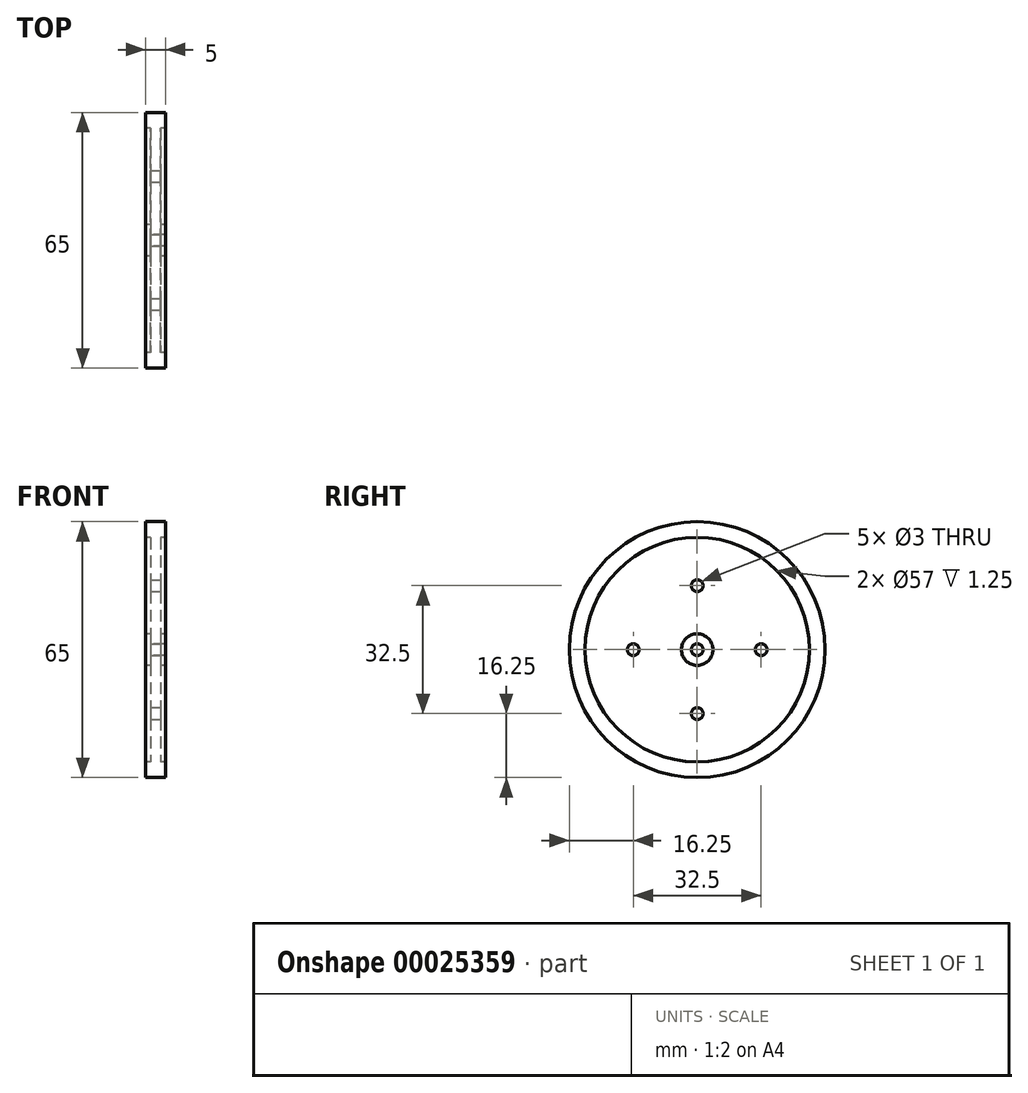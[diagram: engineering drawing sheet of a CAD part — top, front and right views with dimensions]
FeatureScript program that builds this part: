
annotation { "Feature Type Name" : "Feature", "Feature Type Description" : "" }
export const myFeature = defineFeature(function(context is Context, id is Id, definition is map)
    precondition{}
    {
        {
            var Q0;
            Q0=qCreatedBy(makeId("Front.planeOp"),FACE);
            var sketch = newSketch(context, id + "F0", { "sketchPlane" : qUnion([Q0])});
            skLineSegment(sketch, "E0", {"start": v(-50.28, 0) * mm, "end": v(50.2, 0) * mm, "construction": true});
            skLineSegment(sketch, "E1.rect.bottom", {"start": v(2.5, 4) * mm, "end": v(-2.5, 4) * mm});
            skLineSegment(sketch, "E1.rect.top", {"start": v(2.5, 1.5) * mm, "end": v(-2.5, 1.5) * mm});
            skLineSegment(sketch, "E1.rect.left", {"start": v(2.5, 4) * mm, "end": v(2.5, 1.5) * mm});
            skLineSegment(sketch, "E1.rect.right", {"start": v(-2.5, 4) * mm, "end": v(-2.5, 1.5) * mm});
            skPoint(sketch, "E1.rect.middle", {"position": v(0, 2.75) * mm});
            skLineSegment(sketch, "E2.bottom", {"start": v(-1.25, 4) * mm, "end": v(1.25, 4) * mm});
            skLineSegment(sketch, "E2.top", {"start": v(-1.25, 28.5) * mm, "end": v(1.25, 28.5) * mm});
            skLineSegment(sketch, "E2.left", {"start": v(-1.25, 4) * mm, "end": v(-1.25, 28.5) * mm});
            skLineSegment(sketch, "E2.right", {"start": v(1.25, 4) * mm, "end": v(1.25, 28.5) * mm});
            skLineSegment(sketch, "E3.rect.bottom", {"start": v(2.5, 28.5) * mm, "end": v(-2.5, 28.5) * mm});
            skLineSegment(sketch, "E3.rect.top", {"start": v(2.5, 32.5) * mm, "end": v(-2.5, 32.5) * mm});
            skLineSegment(sketch, "E3.rect.left", {"start": v(2.5, 28.5) * mm, "end": v(2.5, 32.5) * mm});
            skLineSegment(sketch, "E3.rect.right", {"start": v(-2.5, 28.5) * mm, "end": v(-2.5, 32.5) * mm});
            skPoint(sketch, "E3.rect.middle", {"position": v(0, 30.5) * mm});
            skSolve(sketch);
        }
        {
            var Q0;
            Q0=qSketchRegion(id+"F0",true);
            var Q1;
            Q1=sQuery(id+"F0.wireOp",EDGE,"E0");
            revolve(context, id + "F1", {"entities" : qUnion([Q0]), "axis" : qUnion([Q1]), "revolveType" : RevolveType.FULL});
        }
        {
            var Q0;
            Q0=makeQuery(id+"F1.opRevolve","SWEPT_FACE",FACE,{"disambiguationData":[OSD([sQuery(id+"F0.wireOp",EDGE,"E3.rect.left")])]});
            var sketch = newSketch(context, id + "F2", { "sketchPlane" : qUnion([Q0])});
            skLineSegment(sketch, "E4", {"start": v(0, 0) * mm, "end": v(0, 32.5) * mm, "construction": true});
            skLineSegment(sketch, "E5", {"start": v(0, 32.5) * mm, "end": v(0, 0) * mm, "construction": true});
            skLineSegment(sketch, "E6", {"start": v(0, 0) * mm, "end": v(0, -32.5) * mm, "construction": true});
            skLineSegment(sketch, "E7", {"start": v(0, -32.5) * mm, "end": v(0, 0) * mm, "construction": true});
            skPoint(sketch, "E8", {"position": v(0, 16.25) * mm});
            skCircle(sketch, "E9", {"center": v(0, 0) * mm, "radius": 16.25 * mm, "construction": true});
            skCircle(sketch, "E10", {"center": v(0, 16.25) * mm, "radius": 1.5 * mm});
            skCircle(sketch, "E11", {"center": v(0, -16.25) * mm, "radius": 1.5 * mm});
            skLineSegment(sketch, "E12", {"start": v(0, 0) * mm, "end": v(-32.5, 0) * mm, "construction": true});
            skLineSegment(sketch, "E13", {"start": v(-32.5, 0) * mm, "end": v(32.5, 0) * mm, "construction": true});
            skCircle(sketch, "E14", {"center": v(-16.25, 0) * mm, "radius": 1.5 * mm});
            skCircle(sketch, "E15", {"center": v(16.25, 0) * mm, "radius": 1.5 * mm});
            skSolve(sketch);
        }
        {
            var Q0;
            Q0=qSketchRegion(id+"F2",true);
            extrude(context, id + "F3", {"entities" : qUnion([Q0]), "operationType" : NewBodyOperationType.REMOVE, "oppositeDirection" : true, "depth" : 25 * mm});
        }
    });
